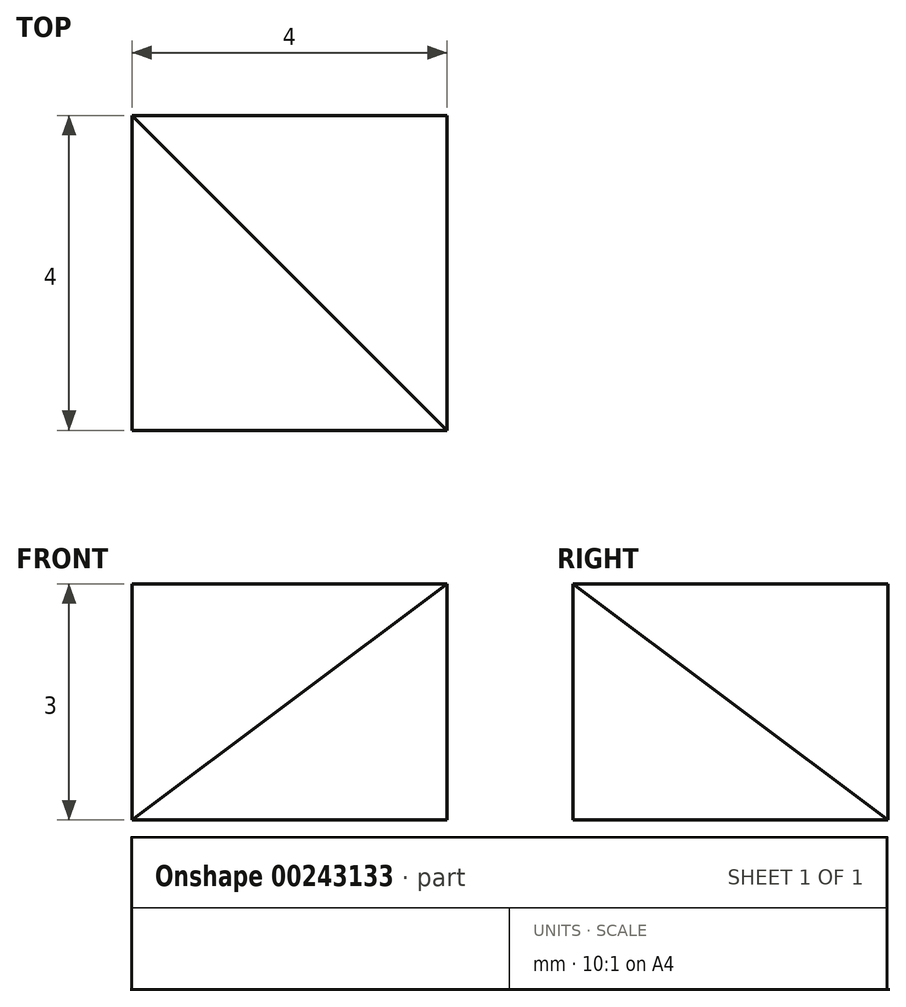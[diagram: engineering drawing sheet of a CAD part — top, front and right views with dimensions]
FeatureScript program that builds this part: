
annotation { "Feature Type Name" : "Feature", "Feature Type Description" : "" }
export const myFeature = defineFeature(function(context is Context, id is Id, definition is map)
    precondition{}
    {
        {
            var Q0;
            Q0=qCreatedBy(makeId("Front.planeOp"),FACE);
            var sketch = newSketch(context, id + "F0", { "sketchPlane" : qUnion([Q0])});
            skLineSegment(sketch, "E0.bottom", {"start": v(0, 0) * mm, "end": v(4, 0) * mm});
            skLineSegment(sketch, "E0.top", {"start": v(0, 3) * mm, "end": v(4, 3) * mm});
            skLineSegment(sketch, "E0.left", {"start": v(0, 0) * mm, "end": v(0, 3) * mm});
            skLineSegment(sketch, "E0.right", {"start": v(4, 0) * mm, "end": v(4, 3) * mm});
            skSolve(sketch);
        }
        {
            var Q0;
            Q0 = qSketchRegion(id + "F0", true);
            extrude(context, id + "F1", {"entities" : qUnion([Q0]), "depth" : 4 * mm});
        }
        {
            var Q0;
            Q0=makeQuery(id+"F1.opExtrude","CAP_VERTEX",VERTEX,{"disambiguationData":[OSD([sQuery(id+"F0.wireOp",EDGE,"E0.top"),sQuery(id+"F0.wireOp",EDGE,"E0.right")])],"isStart":false});
            var Q1;
            Q1=makeQuery(id+"F1.opExtrude","CAP_VERTEX",VERTEX,{"disambiguationData":[OSD([sQuery(id+"F0.wireOp",EDGE,"E0.bottom"),sQuery(id+"F0.wireOp",EDGE,"E0.left")])],"isStart":false});
            var Q2;
            Q2=makeQuery(id+"F1.opExtrude","CAP_VERTEX",VERTEX,{"disambiguationData":[OSD([sQuery(id+"F0.wireOp",EDGE,"E0.top"),sQuery(id+"F0.wireOp",EDGE,"E0.left")])],"isStart":true});
            cPlane(context, id + "F2", {"entities" : qUnion([Q0, Q1, Q2]), "cplaneType" : CPlaneType.THREE_POINT, "offset" : 25 * mm, "width" : 150 * mm, "height" : 150 * mm});
        }
        {
            var Q0;
            Q0=makeQuery(id+"F1.opExtrude","CAP_VERTEX",VERTEX,{"disambiguationData":[OSD([sQuery(id+"F0.wireOp",EDGE,"E0.top"),sQuery(id+"F0.wireOp",EDGE,"E0.left")])],"isStart":true});
            var Q1;
            Q1=makeQuery(id+"F1.opExtrude","CAP_VERTEX",VERTEX,{"disambiguationData":[OSD([sQuery(id+"F0.wireOp",EDGE,"E0.top"),sQuery(id+"F0.wireOp",EDGE,"E0.right")])],"isStart":false});
            var Q2;
            Q2=makeQuery(id+"F1.opExtrude","CAP_VERTEX",VERTEX,{"disambiguationData":[OSD([sQuery(id+"F0.wireOp",EDGE,"E0.bottom"),sQuery(id+"F0.wireOp",EDGE,"E0.right")])],"isStart":true});
            cPlane(context, id + "F3", {"entities" : qUnion([Q0, Q1, Q2]), "cplaneType" : CPlaneType.THREE_POINT, "offset" : 25 * mm, "width" : 150 * mm, "height" : 150 * mm});
        }
        {
            var Q0;
            Q0=qCreatedBy(id+"F2.planeOp",FACE);
            var sketch = newSketch(context, id + "F4", { "sketchPlane" : qUnion([Q0])});
            skPoint(sketch, "E1.0", {"position": v(1.23, 1.8) * mm});
            skPoint(sketch, "E1.1", {"position": v(5.9, -1.4) * mm});
            skPoint(sketch, "E1.2", {"position": v(1.23, -3.2) * mm});
            skLineSegment(sketch, "E2", {"start": v(1.23, 1.8) * mm, "end": v(5.9, -1.4) * mm});
            skLineSegment(sketch, "E3", {"start": v(1.23, -3.2) * mm, "end": v(5.9, -1.4) * mm});
            skLineSegment(sketch, "E4", {"start": v(1.23, 1.8) * mm, "end": v(1.23, -3.2) * mm});
            skSolve(sketch);
        }
        {
            var Q0;
            Q0 = qSketchRegion(id + "F4", true);
            extrude(context, id + "F5", {"entities" : qUnion([Q0]), "operationType" : NewBodyOperationType.REMOVE, "depth" : 25 * mm});
        }
        {
            var Q0;
            Q0=qCreatedBy(id+"F3.planeOp",FACE);
            var sketch = newSketch(context, id + "F6", { "sketchPlane" : qUnion([Q0])});
            skPoint(sketch, "E5.0", {"position": v(3.43, 5) * mm});
            skPoint(sketch, "E5.1", {"position": v(3.43, 0) * mm});
            skPoint(sketch, "E5.2", {"position": v(-1.23, 1.8) * mm});
            skLineSegment(sketch, "E6", {"start": v(-1.23, 1.8) * mm, "end": v(3.43, 5) * mm});
            skLineSegment(sketch, "E7", {"start": v(3.43, 5) * mm, "end": v(3.43, 0) * mm});
            skLineSegment(sketch, "E8", {"start": v(3.43, 0) * mm, "end": v(-1.23, 1.8) * mm});
            skSolve(sketch);
        }
        {
            var Q0;
            Q0 = qSketchRegion(id + "F6", true);
            extrude(context, id + "F7", {"entities" : qUnion([Q0]), "operationType" : NewBodyOperationType.REMOVE, "oppositeDirection" : true, "depth" : 25 * mm});
        }
    });
